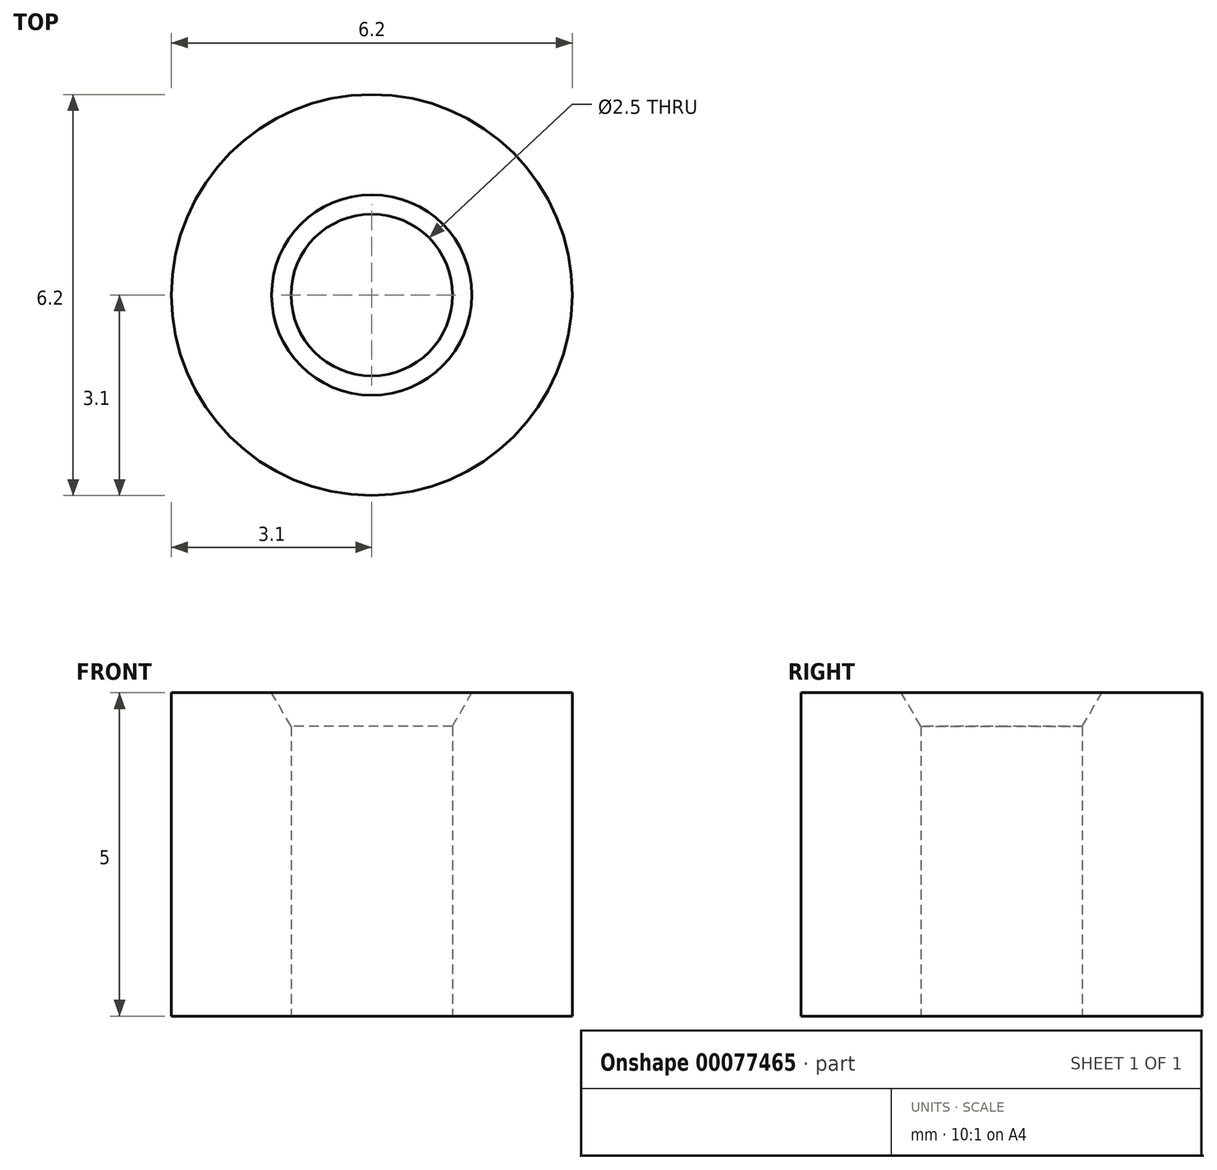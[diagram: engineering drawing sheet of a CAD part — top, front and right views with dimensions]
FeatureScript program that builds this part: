
annotation { "Feature Type Name" : "Feature", "Feature Type Description" : "" }
export const myFeature = defineFeature(function(context is Context, id is Id, definition is map)
    precondition{}
    {
        {
            var Q0;
            Q0=qCreatedBy(makeId("Top.planeOp"),FACE);
            var sketch = newSketch(context, id + "F0", { "sketchPlane" : qUnion([Q0])});
            skCircle(sketch, "E0", {"center": v(0, 0) * mm, "radius": 3.1 * mm});
            skCircle(sketch, "E1", {"center": v(0, 0) * mm, "radius": 1.25 * mm});
            skSolve(sketch);
        }
        {
            var Q0;
            Q0=makeQuery(id+"F0.imprint","IMPRINT",FACE,{"disambiguationData":[TD([[makeQuery(id+"F0.imprint","IMPRINT",EDGE,{"derivedFrom":sQuery(id+"F0.wireOp",EDGE,"E0")}),1.0]])]});
            extrude(context, id + "F1", {"entities" : qUnion([Q0]), "depth" : 5 * mm});
        }
        {
            var Q0;
            Q0=makeQuery(id+"F1.opExtrude","CAP_EDGE",EDGE,{"disambiguationData":[OSD([sQuery(id+"F0.wireOp",EDGE,"E1")])],"isStart":false});
            chamfer(context, id + "F2", {"entities" : qUnion([Q0]), "chamferType" : ChamferType.OFFSET_ANGLE, "width" : 0.3 * mm, "oppositeDirection" : true, "angle" : 60 * degree, "tangentPropagation" : true});
        }
    });
